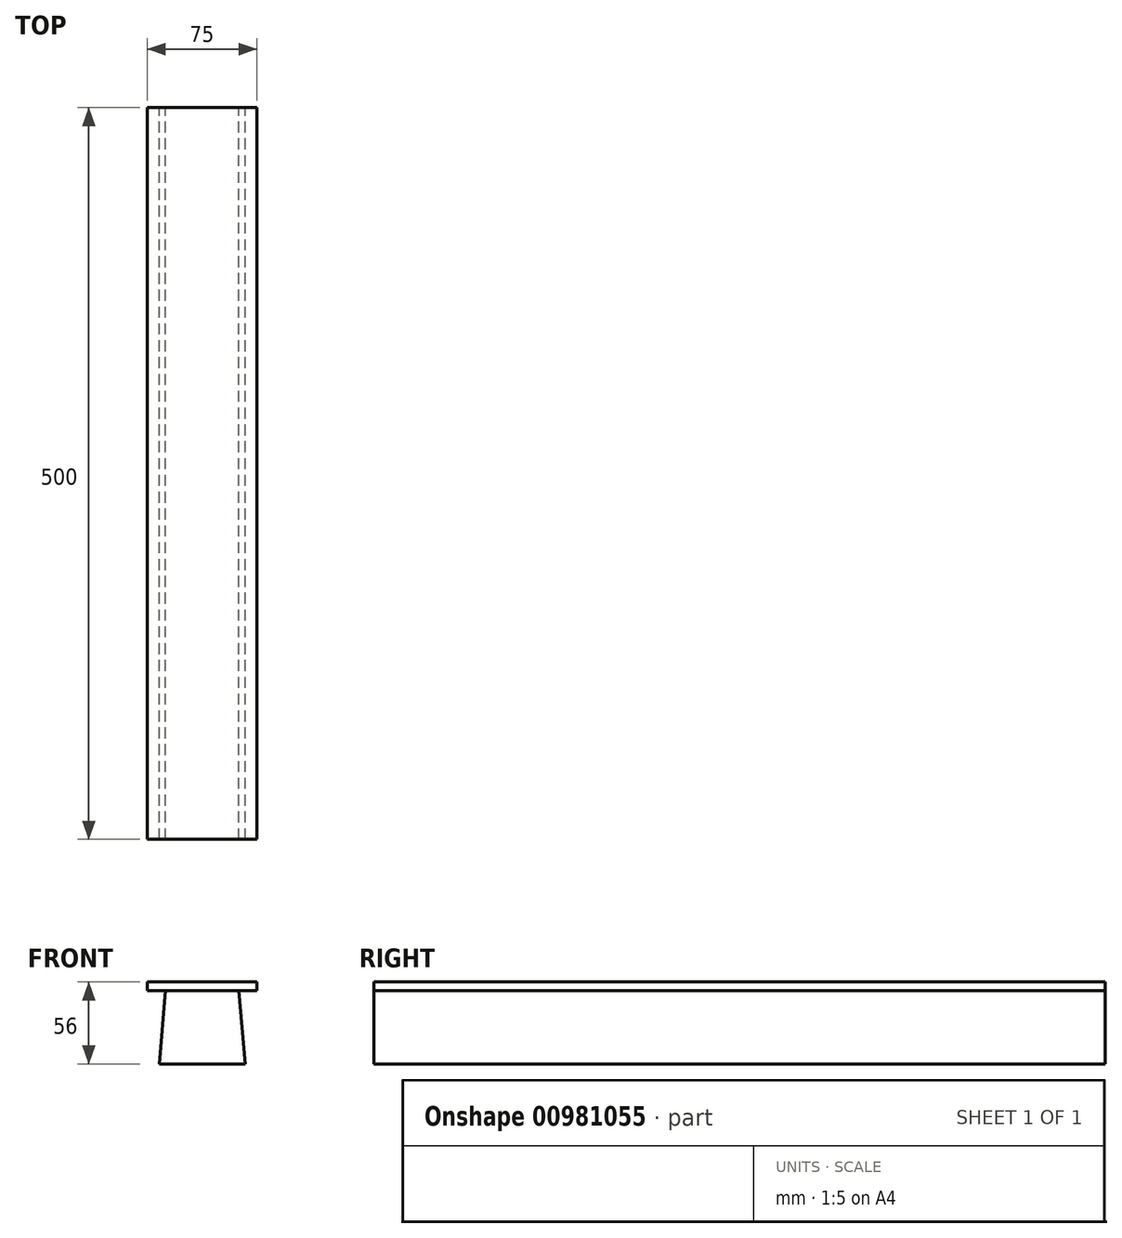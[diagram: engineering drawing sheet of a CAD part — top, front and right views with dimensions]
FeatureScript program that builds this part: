
annotation { "Feature Type Name" : "Feature", "Feature Type Description" : "" }
export const myFeature = defineFeature(function(context is Context, id is Id, definition is map)
    precondition{}
    {
        {
            var Q0;
            Q0=qCreatedBy(makeId("Front.planeOp"),FACE);
            var sketch = newSketch(context, id + "F0", { "sketchPlane" : qUnion([Q0])});
            skLineSegment(sketch, "E0", {"start": v(-29.37, 0) * mm, "end": v(-25, 50) * mm});
            skLineSegment(sketch, "E1", {"start": v(-25, 50) * mm, "end": v(25, 50) * mm});
            skLineSegment(sketch, "E2", {"start": v(25, 50) * mm, "end": v(29.37, 0) * mm});
            skLineSegment(sketch, "E3", {"start": v(29.37, 0) * mm, "end": v(-29.37, 0) * mm});
            skLineSegment(sketch, "E4", {"start": v(0, 0) * mm, "end": v(0, 50) * mm, "construction": true});
            skSolve(sketch);
        }
        {
            var Q0;
            Q0=makeQuery(id+"F0.imprint","IMPRINT",FACE,{"disambiguationData":[TD([[makeQuery(id+"F0.imprint","IMPRINT",EDGE,{"derivedFrom":sQuery(id+"F0.wireOp",EDGE,"E0")}),-1.0]])]});
            extrude(context, id + "F1", {"entities" : qUnion([Q0]), "depth" : 500 * mm, "offsetDistance" : 25 * mm});
        }
        {
            var Q0;
            Q0=qCreatedBy(makeId("Front.planeOp"),FACE);
            var sketch = newSketch(context, id + "F2", { "sketchPlane" : qUnion([Q0])});
            skLineSegment(sketch, "E5.bottom", {"start": v(-37.5, 56) * mm, "end": v(37.5, 56) * mm});
            skLineSegment(sketch, "E5.top", {"start": v(-37.5, 50) * mm, "end": v(37.5, 50) * mm});
            skLineSegment(sketch, "E5.left", {"start": v(-37.5, 56) * mm, "end": v(-37.5, 50) * mm});
            skLineSegment(sketch, "E5.right", {"start": v(37.5, 56) * mm, "end": v(37.5, 50) * mm});
            skSolve(sketch);
        }
        {
            var Q0;
            Q0=makeQuery(id+"F2.imprint","IMPRINT",FACE,{"disambiguationData":[TD([[makeQuery(id+"F2.imprint","IMPRINT",EDGE,{"derivedFrom":sQuery(id+"F2.wireOp",EDGE,"E5.bottom")}),-1.0]])]});
            var Q1;
            Q1=makeQuery(id+"F1.opExtrude","CAP_FACE",FACE,{"disambiguationData":[OSD([sQuery(id+"F0.wireOp",EDGE,"E0"),sQuery(id+"F0.wireOp",EDGE,"E1"),sQuery(id+"F0.wireOp",EDGE,"E2"),sQuery(id+"F0.wireOp",EDGE,"E3")])],"isStart":false});
            extrude(context, id + "F3", {"entities" : qUnion([Q0]), "depth" : 500 * mm, "endBoundEntityFace" : qUnion([Q1]), "offsetDistance" : 25 * mm});
        }
    });
